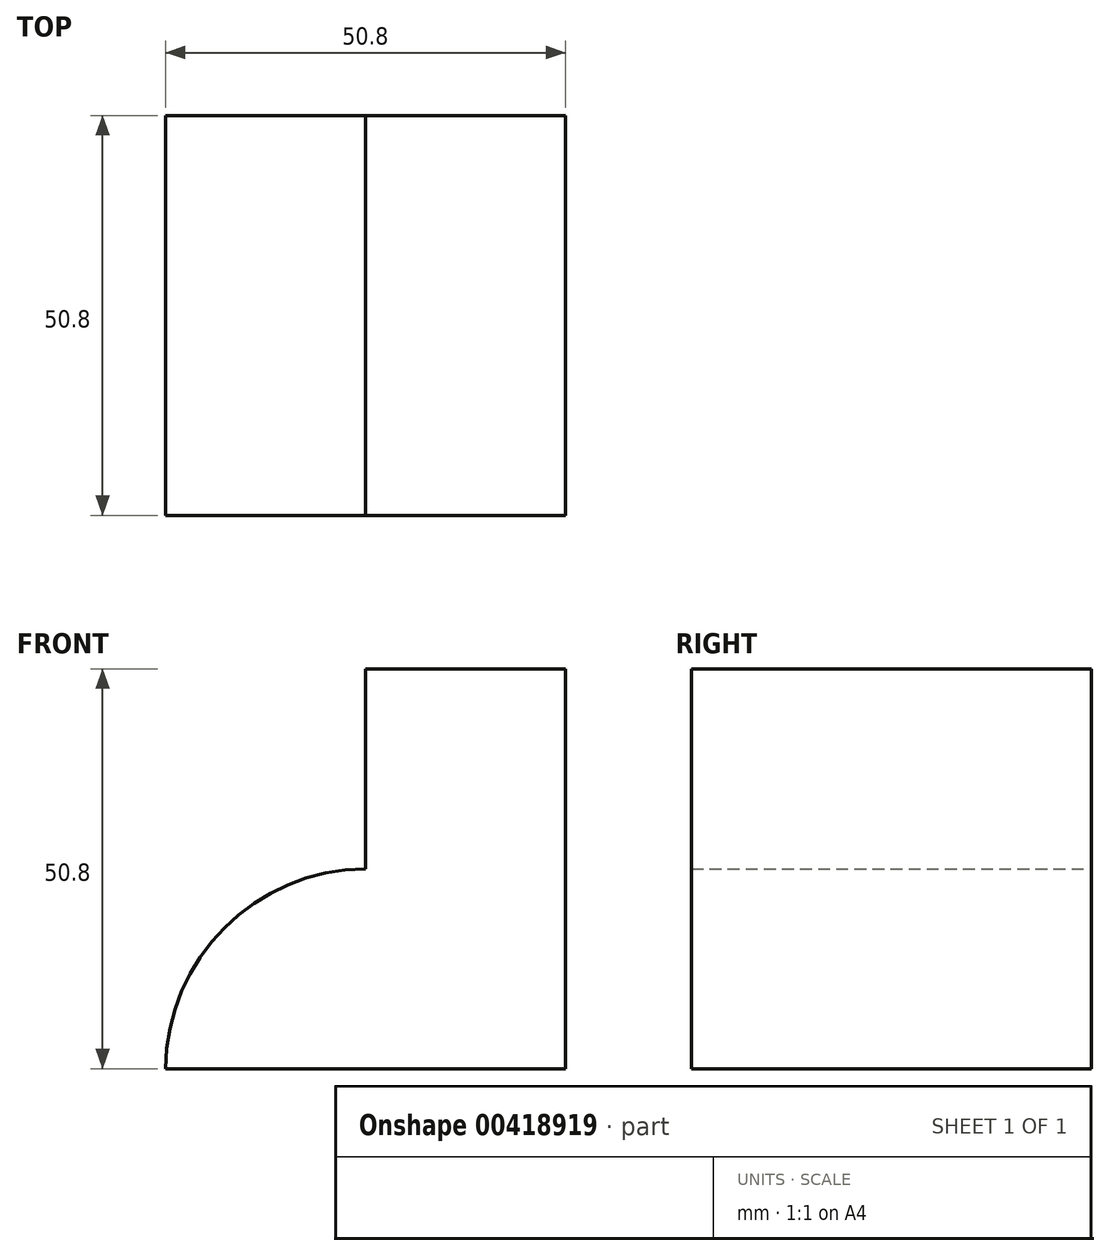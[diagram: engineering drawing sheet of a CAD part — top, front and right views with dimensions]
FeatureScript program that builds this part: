
annotation { "Feature Type Name" : "Feature", "Feature Type Description" : "" }
export const myFeature = defineFeature(function(context is Context, id is Id, definition is map)
    precondition{}
    {
        {
            var Q0;
            Q0=qCreatedBy(makeId("Front.planeOp"),FACE);
            var sketch = newSketch(context, id + "F0", { "sketchPlane" : qUnion([Q0])});
            skLineSegment(sketch, "E0", {"start": v(0, 0) * mm, "end": v(50.8, 0) * mm});
            skLineSegment(sketch, "E1", {"start": v(50.8, 0) * mm, "end": v(50.8, 50.8) * mm});
            skLineSegment(sketch, "E2", {"start": v(50.8, 50.8) * mm, "end": v(25.4, 50.8) * mm});
            skLineSegment(sketch, "E3", {"start": v(25.4, 50.8) * mm, "end": v(25.4, 25.4) * mm});
            skArc(sketch, "E4", {"start": v(25.4, 25.4) * mm, "mid": v(7.5, 17.9) * mm, "end": v(0, 0) * mm});
            skSolve(sketch);
        }
        {
            var Q0;
            Q0=makeQuery(id+"F0.imprint","IMPRINT",FACE,{"disambiguationData":[TD([[makeQuery(id+"F0.imprint","IMPRINT",EDGE,{"derivedFrom":sQuery(id+"F0.wireOp",EDGE,"E0")}),1.0]])]});
            extrude(context, id + "F1", {"entities" : qUnion([Q0]), "depth" : 50.8 * mm});
        }
    });
